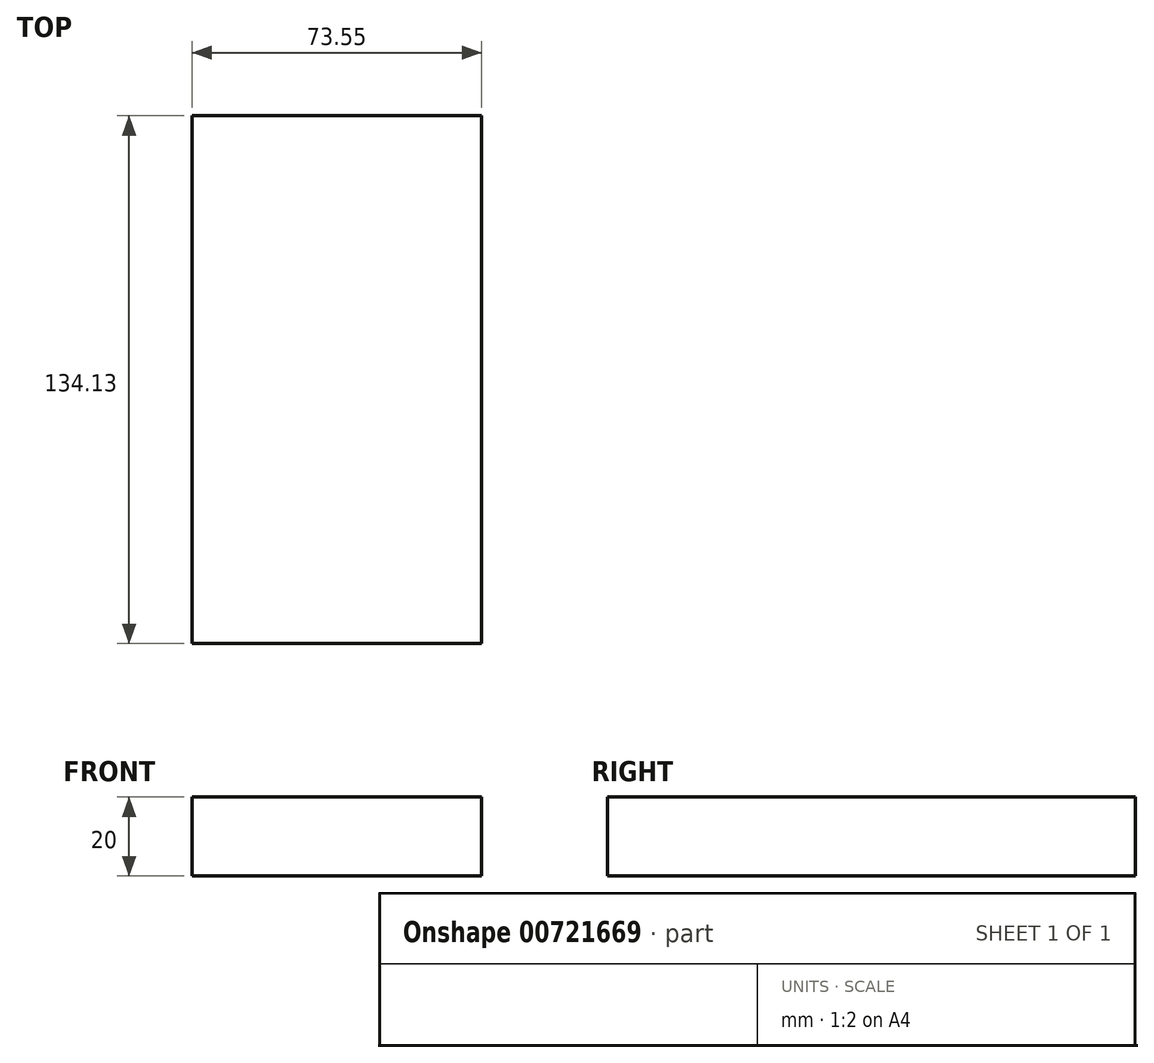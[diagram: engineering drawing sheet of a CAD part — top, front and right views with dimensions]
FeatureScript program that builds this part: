
annotation { "Feature Type Name" : "Feature", "Feature Type Description" : "" }
export const myFeature = defineFeature(function(context is Context, id is Id, definition is map)
    precondition{}
    {
        {
            var Q0;
            Q0=qCreatedBy(makeId("Top.planeOp"),FACE);
            var sketch = newSketch(context, id + "F0", { "sketchPlane" : qUnion([Q0])});
            skLineSegment(sketch, "E0.bottom", {"start": v(0, 0) * mm, "end": v(73.55, 0) * mm});
            skLineSegment(sketch, "E0.top", {"start": v(0, 134.13) * mm, "end": v(73.55, 134.13) * mm});
            skLineSegment(sketch, "E0.left", {"start": v(0, 0) * mm, "end": v(0, 134.13) * mm});
            skLineSegment(sketch, "E0.right", {"start": v(73.55, 0) * mm, "end": v(73.55, 134.13) * mm});
            skSolve(sketch);
        }
        {
            var Q0;
            Q0=makeQuery(id+"F0.imprint","IMPRINT",FACE,{"disambiguationData":[TD([[makeQuery(id+"F0.imprint","IMPRINT",EDGE,{"derivedFrom":sQuery(id+"F0.wireOp",EDGE,"E0.bottom")}),1.0]])]});
            extrude(context, id + "F1", {"entities" : qUnion([Q0]), "depth" : 20 * mm, "offsetDistance" : 25 * mm});
        }
    });
